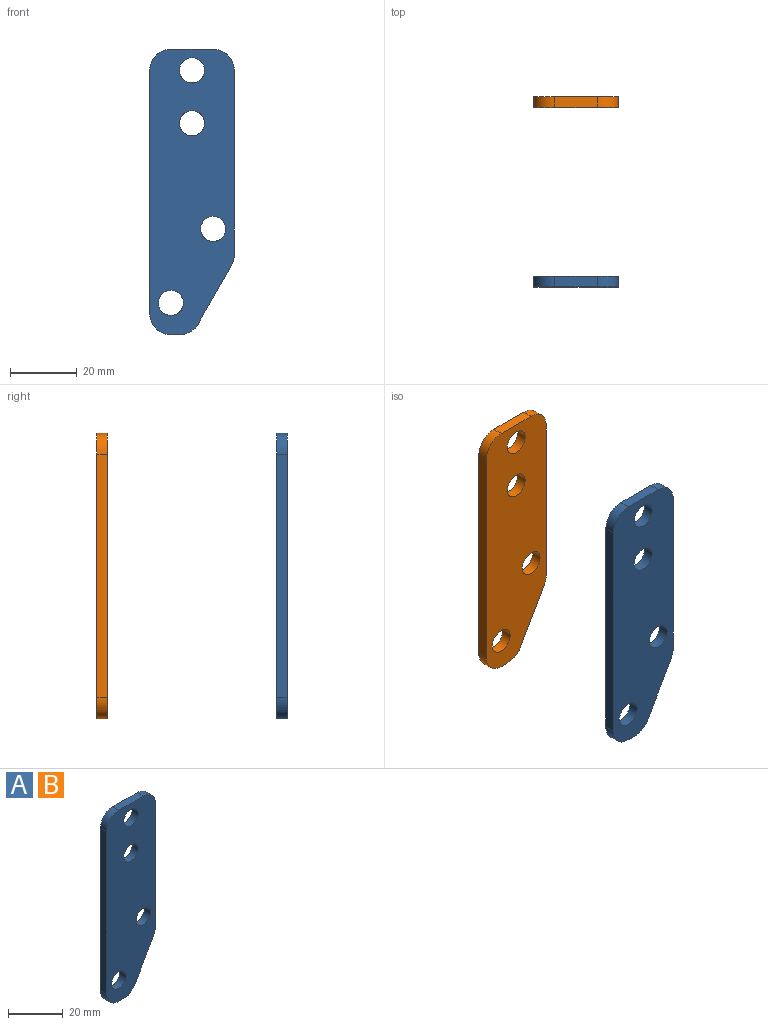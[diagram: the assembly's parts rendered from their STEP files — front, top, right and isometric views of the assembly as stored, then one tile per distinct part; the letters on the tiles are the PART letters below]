
ASSEMBLY  parts=2 mates=1
PART A: 16 faces, bbox 25.4x3.2x85.7 mm
  f0: plane 73.03x3.18mm, normal (-1,0,0), area 231.9mm2, adj f5,f6,f13,f14
  f1: plane 3.18x2.67mm, normal (0,0,-1), area 8.5mm2, adj f5,f6,f14,f15
  f2: plane 17.56x10.04mm, normal (0.87,0,-0.5), area 64.2mm2, adj f5,f6,f11,f15
  f3: plane 55.46x3.18mm, normal (1,0,0), area 176.1mm2, adj f5,f6,f11,f12
  f4: plane 12.7x3.18mm, normal (0,0,1), area 40.3mm2, adj f5,f6,f12,f13
  f5: plane 85.73x25.4mm, normal (0,-1,0), area 1829.1mm2, adj f0,f1,f2,f3,f4,f7,f8,f9
  f6: plane 85.73x25.4mm, normal (0,1,0), area 1829.1mm2, adj f0,f1,f2,f3,f4,f7,f8,f9
  f7: cylinder r=3.77mm len=7.54mm, axis (0,1,0), area 75.2mm2, adj f5,f6
  f8: cylinder r=3.77mm len=7.54mm, axis (0,1,0), area 75.2mm2, adj f5,f6
  f9: cylinder r=3.77mm len=7.54mm, axis (0,1,0), area 75.2mm2, adj f5,f6
  f10: cylinder r=3.77mm len=7.54mm, axis (0,1,0), area 75.2mm2, adj f5,f6
  f11: cylinder r=6.35mm len=3.18mm, axis (0,1,0), area 10.5mm2, adj f2,f3,f5,f6
  f12: cylinder r=6.35mm len=6.35mm, axis (0,-1,0), area 31.7mm2, adj f3,f4,f5,f6
  f13: cylinder r=6.35mm len=6.35mm, axis (0,1,0), area 31.7mm2, adj f0,f4,f5,f6
  f14: cylinder r=6.35mm len=6.35mm, axis (0,-1,0), area 31.7mm2, adj f0,f1,f5,f6
  f15: cylinder r=6.35mm len=5.51mm, axis (0,1,0), area 21.2mm2, adj f1,f2,f5,f6
PART B: same geometry as A
PLACE A t=(-12.23,12.08,-5.31)mm
PLACE B t=(-12.23,66.05,-5.31)mm
MATE fastened B.f7 <-> A.f7  axis (0,-1,0) through (0.47,62.88,51.84)mm
